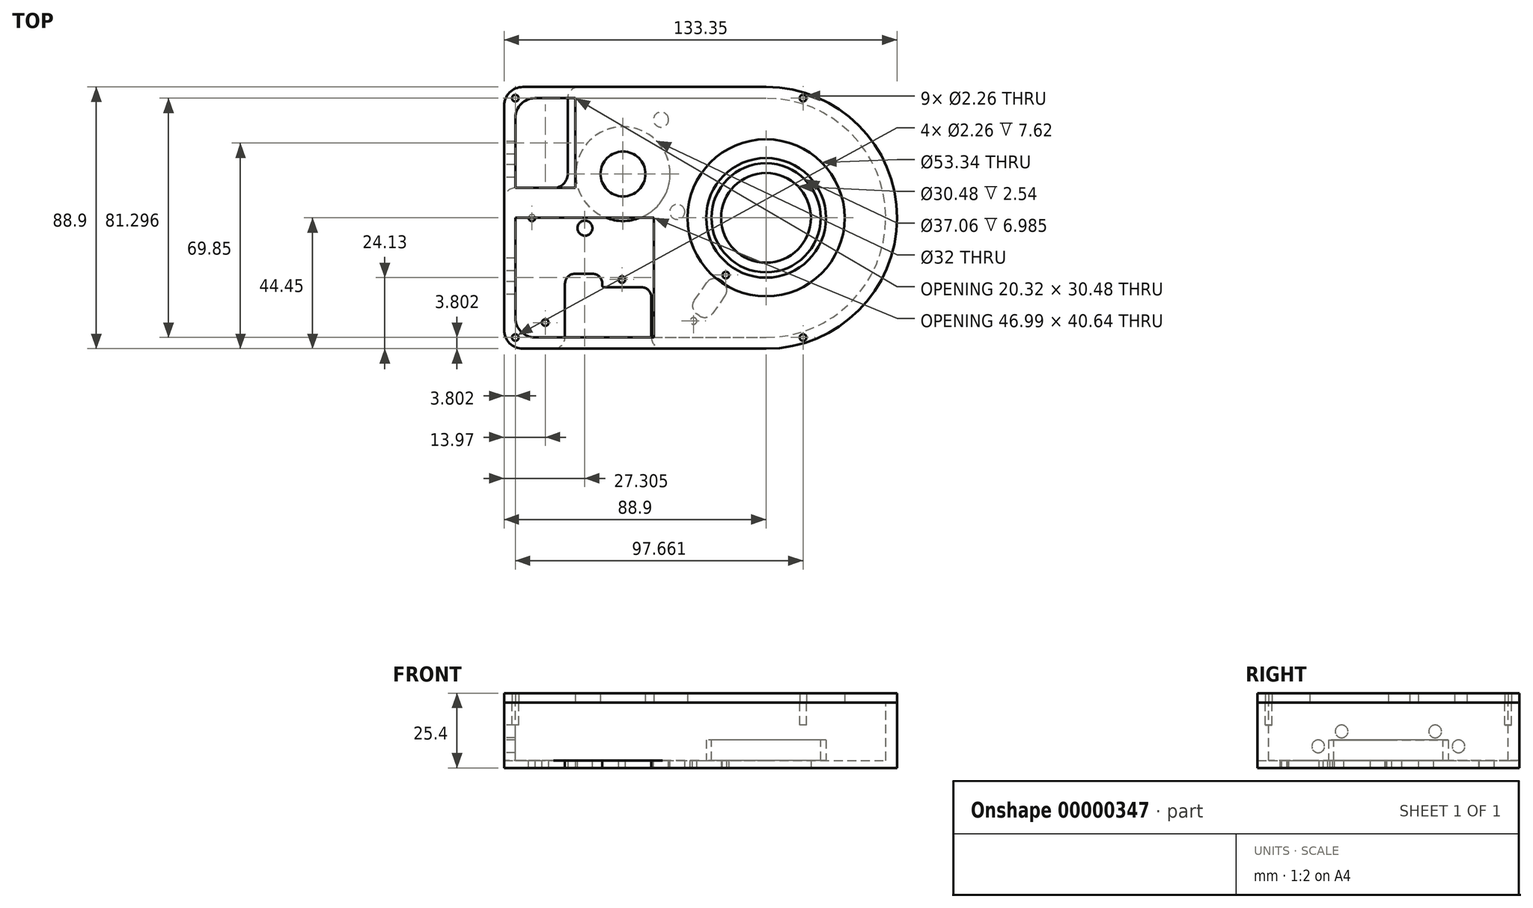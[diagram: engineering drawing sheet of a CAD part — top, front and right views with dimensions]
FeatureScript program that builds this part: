
annotation { "Feature Type Name" : "Feature", "Feature Type Description" : "" }
export const myFeature = defineFeature(function(context is Context, id is Id, definition is map)
    precondition{}
    {
        {
            var Q0;
            Q0=qCreatedBy(makeId("Top.planeOp"),FACE);
            var sketch = newSketch(context, id + "F0", { "sketchPlane" : qUnion([Q0])});
            skLineSegment(sketch, "E0.bottom", {"start": v(6.35, 0) * mm, "end": v(88.9, 0) * mm});
            skLineSegment(sketch, "E0.top", {"start": v(6.35, 88.9) * mm, "end": v(88.9, 88.9) * mm});
            skLineSegment(sketch, "E0.left", {"start": v(0, 6.35) * mm, "end": v(0, 82.55) * mm});
            skLineSegment(sketch, "E0.right", {"start": v(88.9, 0) * mm, "end": v(88.9, 88.9) * mm});
            skArc(sketch, "E1", {"start": v(88.9, 0) * mm, "mid": v(133.35, 44.45) * mm, "end": v(88.9, 88.9) * mm});
            skCircle(sketch, "E2", {"center": v(88.9, 44.45) * mm, "radius": 15.24 * mm});
            skPoint(sketch, "E3.visualSharp", {"position": v(0, 88.9) * mm});
            skArc(sketch, "E3.filletArc", {"start": v(6.35, 88.9) * mm, "mid": v(1.86, 87.04) * mm, "end": v(0, 82.55) * mm});
            skPoint(sketch, "E4.visualSharp", {"position": v(0, 0) * mm});
            skArc(sketch, "E4.filletArc", {"start": v(0, 6.35) * mm, "mid": v(1.86, 1.86) * mm, "end": v(6.35, 0) * mm});
            skSolve(sketch);
        }
        {
            var Q0;
            {var subQ4=sQuery(id+"F0.wireOp",EDGE,"E1");var subQ7=sQuery(id+"F0.wireOp",EDGE,"E0.bottom");Q0=qUnion([makeQuery(id+"F0.imprint","IMPRINT",FACE,{"disambiguationData":[TD([[makeQuery(id+"F0.imprint","IMPRINT",EDGE,{"derivedFrom":subQ7}),1.0]])]}),makeQuery(id+"F0.imprint","IMPRINT",FACE,{"disambiguationData":[TD([[makeQuery(id+"F0.imprint","IMPRINT",EDGE,{"derivedFrom":subQ4}),1.0]])]})]);}
            extrude(context, id + "F1", {"entities" : qUnion([Q0]), "depth" : 22.22 * mm});
        }
        {
            var Q0;
            Q0=makeQuery(id+"F1.opExtrude","CAP_FACE",FACE,{"disambiguationData":[OSD([sQuery(id+"F0.wireOp",EDGE,"E0.bottom"),sQuery(id+"F0.wireOp",EDGE,"E0.top"),sQuery(id+"F0.wireOp",EDGE,"E0.left"),sQuery(id+"F0.wireOp",EDGE,"E1"),sQuery(id+"F0.wireOp",EDGE,"E2")])],"isStart":false});
            var sketch = newSketch(context, id + "F2", { "sketchPlane" : qUnion([Q0])});
            skLineSegment(sketch, "E5.0", {"start": v(10.41, 85.1) * mm, "end": v(88.9, 85.1) * mm});
            skLineSegment(sketch, "E5.1", {"start": v(3.8, 10.41) * mm, "end": v(3.8, 78.49) * mm});
            skLineSegment(sketch, "E5.2", {"start": v(10.41, 3.8) * mm, "end": v(88.9, 3.8) * mm});
            skArc(sketch, "E5.3", {"start": v(88.9, 3.8) * mm, "mid": v(129.54, 44.45) * mm, "end": v(88.9, 85.1) * mm});
            skPoint(sketch, "E6.visualSharp", {"position": v(3.8, 85.1) * mm});
            skArc(sketch, "E6.filletArc", {"start": v(10.41, 85.1) * mm, "mid": v(5.74, 83.16) * mm, "end": v(3.8, 78.49) * mm});
            skPoint(sketch, "E7.visualSharp", {"position": v(3.8, 3.8) * mm});
            skArc(sketch, "E7.filletArc", {"start": v(3.8, 10.41) * mm, "mid": v(5.74, 5.74) * mm, "end": v(10.41, 3.8) * mm});
            skSolve(sketch);
        }
        {
            var Q0;
            {var subQ0=makeQuery(id+"F2.imprint","IMPRINT",EDGE,{"derivedFrom":makeQuery(id+"F1.opExtrude","CAP_EDGE",EDGE,{"disambiguationData":[OSD([sQuery(id+"F0.wireOp",EDGE,"E2")])],"isStart":false})});Q0=qUnion([makeQuery(id+"F2.imprint","IMPRINT",FACE,{"disambiguationData":[TD([[subQ0,1.0]])]}),makeQuery(id+"F2.imprint","IMPRINT",FACE,{"disambiguationData":[TD([[makeQuery(id+"F2.imprint","IMPRINT",EDGE,{"derivedFrom":sQuery(id+"F2.wireOp",EDGE,"E5.0")}),-1.0]])]})]);}
            extrude(context, id + "F3", {"entities" : qUnion([Q0]), "operationType" : NewBodyOperationType.REMOVE, "oppositeDirection" : true, "depth" : 19.68 * mm});
        }
        {
            var Q0;
            Q0=makeQuery(id+"F3.boolean.opBoolean","COPY",FACE,{"derivedFrom":makeQuery(id+"F3.opExtrude","CAP_FACE",FACE,{"disambiguationData":[OSD([sQuery(id+"F2.wireOp",EDGE,"E5.0"),sQuery(id+"F2.wireOp",EDGE,"E5.1"),sQuery(id+"F2.wireOp",EDGE,"E5.2"),sQuery(id+"F2.wireOp",EDGE,"E5.3"),sQuery(id+"F2.wireOp",EDGE,"E6.filletArc"),sQuery(id+"F2.wireOp",EDGE,"E7.filletArc")])],"isStart":false})});
            var sketch = newSketch(context, id + "F4", { "sketchPlane" : qUnion([Q0])});
            skArc(sketch, "E8.0", {"start": v(88.9, 3.8) * mm, "mid": v(129.54, 44.45) * mm, "end": v(88.9, 85.1) * mm, "construction": true});
            skCircle(sketch, "E9", {"center": v(88.9, 44.45) * mm, "radius": 20.32 * mm});
            skSolve(sketch);
        }
        {
            var Q0;
            {var subQ0=makeQuery(id+"F4.imprint","IMPRINT",EDGE,{"derivedFrom":makeQuery(id+"F3.boolean.opBoolean","INTERSECT",EDGE,{"derivedFrom":[makeQuery(id+"F1.opExtrude","SWEPT_FACE",FACE,{"disambiguationData":[OSD([sQuery(id+"F0.wireOp",EDGE,"E2")])]}),makeQuery(id+"F3.opExtrude","CAP_FACE",FACE,{"disambiguationData":[OSD([sQuery(id+"F2.wireOp",EDGE,"E5.0"),sQuery(id+"F2.wireOp",EDGE,"E5.1"),sQuery(id+"F2.wireOp",EDGE,"E5.2"),sQuery(id+"F2.wireOp",EDGE,"E5.3"),sQuery(id+"F2.wireOp",EDGE,"E6.filletArc"),sQuery(id+"F2.wireOp",EDGE,"E7.filletArc")])],"isStart":false})]})});Q0=qUnion([makeQuery(id+"F4.imprint","IMPRINT",FACE,{"disambiguationData":[TD([[subQ0,1.0]])]}),makeQuery(id+"F4.imprint","IMPRINT",FACE,{"disambiguationData":[TD([[makeQuery(id+"F4.imprint","IMPRINT",EDGE,{"derivedFrom":sQuery(id+"F4.wireOp",EDGE,"E9")}),1.0]])]})]);}
            extrude(context, id + "F5", {"entities" : qUnion([Q0]), "operationType" : NewBodyOperationType.ADD, "depth" : 7 * mm});
        }
        {
            var Q0;
            Q0=makeQuery(id+"F5.opExtrude","CAP_FACE",FACE,{"disambiguationData":[OSD([sQuery(id+"F4.wireOp",EDGE,"E9")])],"isStart":false});
            var sketch = newSketch(context, id + "F6", { "sketchPlane" : qUnion([Q0])});
            skCircle(sketch, "E10", {"center": v(88.9, 44.45) * mm, "radius": 18.53 * mm});
            skSolve(sketch);
        }
        {
            var Q0;
            Q0=makeQuery(id+"F6.imprint","IMPRINT",FACE,{"disambiguationData":[TD([[makeQuery(id+"F6.imprint","IMPRINT",EDGE,{"derivedFrom":sQuery(id+"F6.wireOp",EDGE,"E10")}),1.0]])]});
            extrude(context, id + "F7", {"entities" : qUnion([Q0]), "operationType" : NewBodyOperationType.REMOVE, "oppositeDirection" : true, "depth" : 7 * mm});
        }
        {
            var Q0;
            Q0=makeQuery(id+"F1.opExtrude","CAP_FACE",FACE,{"disambiguationData":[OSD([sQuery(id+"F0.wireOp",EDGE,"E0.bottom"),sQuery(id+"F0.wireOp",EDGE,"E0.top"),sQuery(id+"F0.wireOp",EDGE,"E0.left"),sQuery(id+"F0.wireOp",EDGE,"E1"),sQuery(id+"F0.wireOp",EDGE,"E2")])],"isStart":false});
            var sketch = newSketch(context, id + "F8", { "sketchPlane" : qUnion([Q0])});
            skLineSegment(sketch, "E11", {"start": v(101.46, 85.1) * mm, "end": v(101.46, 3.8) * mm, "construction": true});
            skCircle(sketch, "E12", {"center": v(101.46, 3.8) * mm, "radius": 1.13 * mm});
            skCircle(sketch, "E13", {"center": v(101.46, 85.1) * mm, "radius": 1.13 * mm});
            skCircle(sketch, "E14", {"center": v(3.8, 85.1) * mm, "radius": 1.13 * mm});
            skCircle(sketch, "E15", {"center": v(3.8, 3.8) * mm, "radius": 1.13 * mm});
            skLineSegment(sketch, "E16", {"start": v(1.86, 87.04) * mm, "end": v(5.74, 83.16) * mm, "construction": true});
            skLineSegment(sketch, "E17", {"start": v(1.86, 1.86) * mm, "end": v(5.74, 5.74) * mm, "construction": true});
            skLineSegment(sketch, "E18", {"start": v(3.8, 85.1) * mm, "end": v(101.46, 85.1) * mm, "construction": true});
            skLineSegment(sketch, "E19", {"start": v(3.8, 3.8) * mm, "end": v(101.46, 3.8) * mm, "construction": true});
            skSolve(sketch);
        }
        {
            var Q0;
            Q0 = qSketchRegion(id + "F8", true);
            extrude(context, id + "F9", {"entities" : qUnion([Q0]), "operationType" : NewBodyOperationType.REMOVE, "oppositeDirection" : true, "depth" : 7.62 * mm});
        }
        {
            var Q0;
            Q0=makeQuery(id+"F3.boolean.opBoolean","COPY",FACE,{"derivedFrom":makeQuery(id+"F3.opExtrude","CAP_FACE",FACE,{"disambiguationData":[OSD([sQuery(id+"F2.wireOp",EDGE,"E5.0"),sQuery(id+"F2.wireOp",EDGE,"E5.1"),sQuery(id+"F2.wireOp",EDGE,"E5.2"),sQuery(id+"F2.wireOp",EDGE,"E5.3"),sQuery(id+"F2.wireOp",EDGE,"E6.filletArc"),sQuery(id+"F2.wireOp",EDGE,"E7.filletArc")])],"isStart":false})});
            var sketch = newSketch(context, id + "F10", { "sketchPlane" : qUnion([Q0])});
            skCircle(sketch, "E20", {"center": v(88.9, 44.45) * mm, "radius": 38.1 * mm, "construction": true});
            skCircle(sketch, "E21", {"center": v(40.34, 59.37) * mm, "radius": 12.7 * mm, "construction": true});
            skCircle(sketch, "E22", {"center": v(40.34, 59.37) * mm, "radius": 16 * mm});
            skCircle(sketch, "E23", {"center": v(40.34, 59.37) * mm, "radius": 22.5 * mm, "construction": true});
            skCircle(sketch, "E24", {"center": v(40.34, 59.37) * mm, "radius": 28.58 * mm, "construction": true});
            skLineSegment(sketch, "E25", {"start": v(21.91, 72.28) * mm, "end": v(58.77, 46.47) * mm, "construction": true});
            skLineSegment(sketch, "E26", {"start": v(27.43, 40.95) * mm, "end": v(53.25, 77.8) * mm, "construction": true});
            skCircle(sketch, "E27", {"center": v(53.25, 77.8) * mm, "radius": 2.55 * mm});
            skCircle(sketch, "E28", {"center": v(21.91, 72.28) * mm, "radius": 2.55 * mm, "construction": true});
            skCircle(sketch, "E29", {"center": v(27.43, 40.95) * mm, "radius": 2.55 * mm});
            skCircle(sketch, "E30", {"center": v(58.77, 46.47) * mm, "radius": 2.55 * mm});
            skLineSegment(sketch, "E31", {"start": v(88.9, 44.45) * mm, "end": v(61.6, 5.58) * mm, "construction": true});
            skCircle(sketch, "E32", {"center": v(75.25, 25.02) * mm, "radius": 1.13 * mm});
            skCircle(sketch, "E33", {"center": v(64.3, 9.43) * mm, "radius": 1.13 * mm});
            skLineSegment(sketch, "E34", {"start": v(60.1, 8.97) * mm, "end": v(74.26, 29.13) * mm, "construction": true});
            skLineSegment(sketch, "E35", {"start": v(74.26, 29.13) * mm, "end": v(79.45, 25.48) * mm, "construction": true});
            skLineSegment(sketch, "E36", {"start": v(79.45, 25.48) * mm, "end": v(65.29, 5.32) * mm, "construction": true});
            skLineSegment(sketch, "E37", {"start": v(65.29, 5.32) * mm, "end": v(60.1, 8.97) * mm, "construction": true});
            skLineSegment(sketch, "E38", {"start": v(72.37, 15.4) * mm, "end": v(67.17, 19.05) * mm, "construction": true});
            skLineSegment(sketch, "E39", {"start": v(64.54, 16.4) * mm, "end": v(68.77, 22.43) * mm});
            skLineSegment(sketch, "E40", {"start": v(73.37, 23.23) * mm, "end": v(74.2, 22.65) * mm});
            skLineSegment(sketch, "E41", {"start": v(75, 18.05) * mm, "end": v(70.77, 12.02) * mm});
            skLineSegment(sketch, "E42", {"start": v(66.17, 11.22) * mm, "end": v(65.34, 11.8) * mm});
            skPoint(sketch, "E43.visualSharp", {"position": v(70.67, 25.13) * mm});
            skArc(sketch, "E43.filletArc", {"start": v(73.37, 23.23) * mm, "mid": v(70.9, 23.78) * mm, "end": v(68.77, 22.43) * mm});
            skPoint(sketch, "E44.visualSharp", {"position": v(76.9, 20.75) * mm});
            skArc(sketch, "E44.filletArc", {"start": v(75, 18.05) * mm, "mid": v(75.56, 20.51) * mm, "end": v(74.2, 22.65) * mm});
            skPoint(sketch, "E45.visualSharp", {"position": v(68.87, 9.32) * mm});
            skArc(sketch, "E45.filletArc", {"start": v(66.17, 11.22) * mm, "mid": v(68.64, 10.66) * mm, "end": v(70.77, 12.02) * mm});
            skPoint(sketch, "E46.visualSharp", {"position": v(62.64, 13.7) * mm});
            skArc(sketch, "E46.filletArc", {"start": v(64.54, 16.4) * mm, "mid": v(63.99, 13.93) * mm, "end": v(65.34, 11.8) * mm});
            skSolve(sketch);
        }
        {
            var Q0;
            Q0 = qSketchRegion(id + "F10", true);
            extrude(context, id + "F11", {"entities" : qUnion([Q0]), "operationType" : NewBodyOperationType.REMOVE, "oppositeDirection" : true, "depth" : 25.4 * mm});
        }
        {
            var Q0;
            Q0=makeQuery(id+"F1.opExtrude","CAP_FACE",FACE,{"disambiguationData":[OSD([sQuery(id+"F0.wireOp",EDGE,"E0.bottom"),sQuery(id+"F0.wireOp",EDGE,"E0.top"),sQuery(id+"F0.wireOp",EDGE,"E0.left"),sQuery(id+"F0.wireOp",EDGE,"E1"),sQuery(id+"F0.wireOp",EDGE,"E2")])],"isStart":false});
            var sketch = newSketch(context, id + "F12", { "sketchPlane" : qUnion([Q0])});
            skLineSegment(sketch, "E47.0", {"start": v(6.35, 88.9) * mm, "end": v(88.9, 88.9) * mm});
            skArc(sketch, "E48.0", {"start": v(88.9, 0) * mm, "mid": v(133.35, 44.45) * mm, "end": v(88.9, 88.9) * mm});
            skLineSegment(sketch, "E49.0", {"start": v(6.35, 0) * mm, "end": v(88.9, 0) * mm});
            skArc(sketch, "E50.0", {"start": v(0, 6.35) * mm, "mid": v(1.86, 1.86) * mm, "end": v(6.35, 0) * mm});
            skLineSegment(sketch, "E51.0", {"start": v(0, 6.35) * mm, "end": v(0, 82.55) * mm});
            skArc(sketch, "E52.0", {"start": v(6.35, 88.9) * mm, "mid": v(1.86, 87.04) * mm, "end": v(0, 82.55) * mm});
            skCircle(sketch, "E53.0", {"center": v(3.8, 85.1) * mm, "radius": 1.13 * mm});
            skCircle(sketch, "E54.0", {"center": v(101.46, 85.1) * mm, "radius": 1.13 * mm});
            skLineSegment(sketch, "E55.0.3", {"start": v(88.9, 88.9) * mm, "end": v(6.35, 88.9) * mm});
            skLineSegment(sketch, "E55.0.5", {"start": v(0, 82.55) * mm, "end": v(0, 6.35) * mm});
            skCircle(sketch, "E56.0", {"center": v(101.46, 3.8) * mm, "radius": 1.13 * mm});
            skCircle(sketch, "E57.0", {"center": v(3.8, 3.8) * mm, "radius": 1.13 * mm});
            skCircle(sketch, "E58", {"center": v(88.9, 44.45) * mm, "radius": 26.67 * mm});
            skCircle(sketch, "E59", {"center": v(40.34, 59.37) * mm, "radius": 7.62 * mm});
            skLineSegment(sketch, "E60.0", {"start": v(10.41, 3.8) * mm, "end": v(88.9, 3.8) * mm});
            skArc(sketch, "E61.0", {"start": v(3.8, 10.41) * mm, "mid": v(5.74, 5.74) * mm, "end": v(10.41, 3.8) * mm});
            skLineSegment(sketch, "E62.0", {"start": v(3.8, 10.41) * mm, "end": v(3.8, 78.49) * mm});
            skArc(sketch, "E63.0", {"start": v(10.41, 85.1) * mm, "mid": v(5.74, 83.16) * mm, "end": v(3.8, 78.49) * mm});
            skLineSegment(sketch, "E64.0", {"start": v(10.41, 85.1) * mm, "end": v(88.9, 85.1) * mm});
            skLineSegment(sketch, "E65", {"start": v(3.8, 44.45) * mm, "end": v(50.8, 44.45) * mm});
            skLineSegment(sketch, "E66", {"start": v(50.8, 44.45) * mm, "end": v(50.8, 3.8) * mm});
            skCircle(sketch, "E67", {"center": v(88.9, 44.45) * mm, "radius": 38.1 * mm, "construction": true});
            skLineSegment(sketch, "E68", {"start": v(3.8, 54.61) * mm, "end": v(24.13, 54.61) * mm});
            skLineSegment(sketch, "E69", {"start": v(24.13, 54.61) * mm, "end": v(24.13, 85.1) * mm});
            skSolve(sketch);
        }
        {
            var Q0;
            Q0 = qSketchRegion(id + "F12", true);
            extrude(context, id + "F13", {"entities" : qUnion([Q0]), "depth" : 3.17 * mm});
        }
        {
            var Q0;
            Q0=makeQuery(id+"F1.opExtrude","SWEPT_FACE",FACE,{"disambiguationData":[OSD([sQuery(id+"F0.wireOp",EDGE,"E0.left")])]});
            var sketch = newSketch(context, id + "F14", { "sketchPlane" : qUnion([Q0])});
            skCircle(sketch, "E70", {"center": v(-68.26, 7.3) * mm, "radius": 2.16 * mm});
            skCircle(sketch, "E71", {"center": v(-20.64, 7.3) * mm, "radius": 2.16 * mm});
            skCircle(sketch, "E72", {"center": v(-60.33, 12.38) * mm, "radius": 2.16 * mm});
            skCircle(sketch, "E73", {"center": v(-28.58, 12.38) * mm, "radius": 2.16 * mm});
            skSolve(sketch);
        }
        {
            var Q0;
            {Q0=qUnion([makeQuery(id+"F14.imprint","IMPRINT",FACE,{"disambiguationData":[TD([[makeQuery(id+"F14.imprint","IMPRINT",EDGE,{"derivedFrom":sQuery(id+"F14.wireOp",EDGE,"E70")}),1.0]])]}),makeQuery(id+"F14.imprint","IMPRINT",FACE,{"disambiguationData":[TD([[makeQuery(id+"F14.imprint","IMPRINT",EDGE,{"derivedFrom":sQuery(id+"F14.wireOp",EDGE,"E71")}),1.0]])]}),makeQuery(id+"F14.imprint","IMPRINT",FACE,{"disambiguationData":[TD([[makeQuery(id+"F14.imprint","IMPRINT",EDGE,{"derivedFrom":sQuery(id+"F14.wireOp",EDGE,"E72")}),1.0]])]}),makeQuery(id+"F14.imprint","IMPRINT",FACE,{"disambiguationData":[TD([[makeQuery(id+"F14.imprint","IMPRINT",EDGE,{"derivedFrom":sQuery(id+"F14.wireOp",EDGE,"E73")}),1.0]])]})]);}
            var Q1;
            Q1=makeQuery(id+"F3.boolean.opBoolean","COPY",FACE,{"derivedFrom":makeQuery(id+"F3.opExtrude","SWEPT_FACE",FACE,{"disambiguationData":[OSD([sQuery(id+"F2.wireOp",EDGE,"E5.1")])]})});
            extrude(context, id + "F15", {"entities" : qUnion([Q0]), "operationType" : NewBodyOperationType.REMOVE, "endBound" : BoundingType.UP_TO_SURFACE, "oppositeDirection" : true, "endBoundEntityFace" : qUnion([Q1]), "depth" : 25.4 * mm});
        }
        {
            var Q0;
            Q0=makeQuery(id+"F1.opExtrude","CAP_FACE",FACE,{"disambiguationData":[OSD([sQuery(id+"F0.wireOp",EDGE,"E0.bottom"),sQuery(id+"F0.wireOp",EDGE,"E0.top"),sQuery(id+"F0.wireOp",EDGE,"E0.left"),sQuery(id+"F0.wireOp",EDGE,"E1"),sQuery(id+"F0.wireOp",EDGE,"E2")])],"isStart":true});
            var sketch = newSketch(context, id + "F16", { "sketchPlane" : qUnion([Q0])});
            skCircle(sketch, "E74", {"center": v(88.9, -44.45) * mm, "radius": 28.57 * mm, "construction": true});
            skLineSegment(sketch, "E75.bottom", {"start": v(60.32, -73.03) * mm, "end": v(117.47, -73.03) * mm, "construction": true});
            skLineSegment(sketch, "E75.top", {"start": v(60.32, -15.88) * mm, "end": v(117.47, -15.88) * mm, "construction": true});
            skLineSegment(sketch, "E75.left", {"start": v(60.32, -73.03) * mm, "end": v(60.32, -15.88) * mm, "construction": true});
            skLineSegment(sketch, "E75.right", {"start": v(117.47, -73.03) * mm, "end": v(117.47, -15.88) * mm, "construction": true});
            skCircle(sketch, "E76", {"center": v(65.09, -68.26) * mm, "radius": 2.16 * mm});
            skCircle(sketch, "E77", {"center": v(65.09, -20.64) * mm, "radius": 2.16 * mm});
            skSolve(sketch);
        }
        {
            var Q0;
            Q0=makeQuery(id+"F3.boolean.opBoolean","COPY",FACE,{"derivedFrom":makeQuery(id+"F3.opExtrude","CAP_FACE",FACE,{"disambiguationData":[OSD([sQuery(id+"F2.wireOp",EDGE,"E5.0"),sQuery(id+"F2.wireOp",EDGE,"E5.1"),sQuery(id+"F2.wireOp",EDGE,"E5.2"),sQuery(id+"F2.wireOp",EDGE,"E5.3"),sQuery(id+"F2.wireOp",EDGE,"E6.filletArc"),sQuery(id+"F2.wireOp",EDGE,"E7.filletArc")])],"isStart":false})});
            var sketch = newSketch(context, id + "F17", { "sketchPlane" : qUnion([Q0])});
            skCircle(sketch, "E78", {"center": v(9.45, 44.45) * mm, "radius": 1.13 * mm});
            skCircle(sketch, "E79.cCircle", {"center": v(9.45, 44.45) * mm, "radius": 3.67 * mm, "construction": true});
            skLineSegment(sketch, "E79.0", {"start": v(12.07, 41.89) * mm, "end": v(8.54, 40.9) * mm, "construction": true});
            skLineSegment(sketch, "E79.1", {"start": v(8.54, 40.9) * mm, "end": v(5.92, 43.46) * mm, "construction": true});
            skLineSegment(sketch, "E79.2", {"start": v(5.92, 43.46) * mm, "end": v(6.83, 47.01) * mm, "construction": true});
            skLineSegment(sketch, "E79.3", {"start": v(6.83, 47.01) * mm, "end": v(10.36, 48) * mm, "construction": true});
            skLineSegment(sketch, "E79.4", {"start": v(10.36, 48) * mm, "end": v(12.98, 45.44) * mm, "construction": true});
            skLineSegment(sketch, "E79.5", {"start": v(12.98, 45.44) * mm, "end": v(12.07, 41.89) * mm, "construction": true});
            skCircle(sketch, "E80", {"center": v(13.96, 8.86) * mm, "radius": 1.13 * mm});
            skCircle(sketch, "E81", {"center": v(40, 23.48) * mm, "radius": 1.13 * mm});
            skSolve(sketch);
        }
        {
            var Q0;
            Q0 = qSketchRegion(id + "F17", true);
            extrude(context, id + "F18", {"entities" : qUnion([Q0]), "operationType" : NewBodyOperationType.REMOVE, "endBound" : BoundingType.THROUGH_ALL, "oppositeDirection" : true, "depth" : 25.4 * mm});
        }
        {
            var Q0;
            Q0=makeQuery(id+"F1.opExtrude","CAP_FACE",FACE,{"disambiguationData":[OSD([sQuery(id+"F0.wireOp",EDGE,"E0.bottom"),sQuery(id+"F0.wireOp",EDGE,"E0.top"),sQuery(id+"F0.wireOp",EDGE,"E0.left"),sQuery(id+"F0.wireOp",EDGE,"E1"),sQuery(id+"F0.wireOp",EDGE,"E2"),sQuery(id+"F0.wireOp",EDGE,"E3.filletArc"),sQuery(id+"F0.wireOp",EDGE,"E4.filletArc")])],"isStart":true});
            var sketch = newSketch(context, id + "F19", { "sketchPlane" : qUnion([Q0])});
            skLineSegment(sketch, "E82.top", {"start": v(16.76, -54.61) * mm, "end": v(3.8, -54.61) * mm});
            skLineSegment(sketch, "E82.left", {"start": v(21.59, -85.1) * mm, "end": v(21.59, -59.44) * mm});
            skLineSegment(sketch, "E83.0", {"start": v(21.59, -85.1) * mm, "end": v(88.9, -85.1) * mm, "construction": true});
            skLineSegment(sketch, "E84.0", {"start": v(10.41, -3.8) * mm, "end": v(88.9, -3.8) * mm, "construction": true});
            skLineSegment(sketch, "E85.0", {"start": v(3.8, -10.41) * mm, "end": v(3.8, -54.61) * mm, "construction": true});
            skLineSegment(sketch, "E86", {"start": v(25.4, -88.9) * mm, "end": v(25.4, -88.9) * mm});
            skLineSegment(sketch, "E87", {"start": v(0, -50.8) * mm, "end": v(0, -50.8) * mm});
            skLineSegment(sketch, "E88", {"start": v(21.59, -85.1) * mm, "end": v(21.59, -85.1) * mm});
            skLineSegment(sketch, "E89", {"start": v(3.8, -54.61) * mm, "end": v(3.81, -54.61) * mm});
            skPoint(sketch, "E90.orphan", {"position": v(3.8, -78.49) * mm});
            skLineSegment(sketch, "E91.0", {"start": v(0, -50.8) * mm, "end": v(0, -82.55) * mm});
            skArc(sketch, "E92.0", {"start": v(6.35, -88.9) * mm, "mid": v(1.86, -87.04) * mm, "end": v(0, -82.55) * mm});
            skLineSegment(sketch, "E93.0", {"start": v(6.35, -88.9) * mm, "end": v(25.4, -88.9) * mm});
            skPoint(sketch, "E94.orphan", {"position": v(0, -6.35) * mm});
            skPoint(sketch, "E95.orphan", {"position": v(88.9, -88.9) * mm});
            skPoint(sketch, "E82.bottom.end.orphan", {"position": v(10.41, -85.1) * mm});
            skPoint(sketch, "E96.visualSharp", {"position": v(0, -54.61) * mm});
            skArc(sketch, "E96.filletArc", {"start": v(0, -50.8) * mm, "mid": v(1.12, -53.5) * mm, "end": v(3.81, -54.61) * mm});
            skPoint(sketch, "E97.visualSharp", {"position": v(21.59, -88.9) * mm});
            skArc(sketch, "E97.filletArc", {"start": v(21.59, -85.1) * mm, "mid": v(22.7, -87.78) * mm, "end": v(25.4, -88.9) * mm});
            skPoint(sketch, "E98.visualSharp", {"position": v(21.59, -54.61) * mm});
            skArc(sketch, "E98.filletArc", {"start": v(21.59, -59.44) * mm, "mid": v(20.18, -56.02) * mm, "end": v(16.76, -54.61) * mm});
            skLineSegment(sketch, "E99.bottom", {"start": v(20.65, 0) * mm, "end": v(49.99, 0) * mm});
            skLineSegment(sketch, "E99.top", {"start": v(33.86, -20.83) * mm, "end": v(46.69, -20.83) * mm});
            skLineSegment(sketch, "E99.left", {"start": v(20.65, -3.8) * mm, "end": v(20.65, -20.83) * mm});
            skLineSegment(sketch, "E99.right", {"start": v(49.99, -3.81) * mm, "end": v(49.99, -17.53) * mm});
            skLineSegment(sketch, "E100.top", {"start": v(23.95, -25.4) * mm, "end": v(30.05, -25.4) * mm});
            skLineSegment(sketch, "E100.left", {"start": v(20.65, -20.83) * mm, "end": v(20.65, -22.1) * mm});
            skLineSegment(sketch, "E100.right", {"start": v(33.35, -21.34) * mm, "end": v(33.35, -22.1) * mm});
            skPoint(sketch, "E101.visualSharp", {"position": v(20.65, -25.4) * mm});
            skArc(sketch, "E101.filletArc", {"start": v(20.65, -22.1) * mm, "mid": v(21.62, -24.43) * mm, "end": v(23.95, -25.4) * mm});
            skPoint(sketch, "E102.visualSharp", {"position": v(33.35, -25.4) * mm});
            skArc(sketch, "E102.filletArc", {"start": v(30.05, -25.4) * mm, "mid": v(32.38, -24.43) * mm, "end": v(33.35, -22.1) * mm});
            skLineSegment(sketch, "E103", {"start": v(16.84, 0) * mm, "end": v(16.84, 0) * mm});
            skLineSegment(sketch, "E104", {"start": v(53.8, 0) * mm, "end": v(53.8, 0) * mm});
            skPoint(sketch, "E105.visualSharp", {"position": v(20.65, 0) * mm});
            skArc(sketch, "E105.filletArc", {"start": v(20.65, -3.8) * mm, "mid": v(19.53, -1.12) * mm, "end": v(16.84, 0) * mm});
            skPoint(sketch, "E106.visualSharp", {"position": v(49.99, 0) * mm});
            skArc(sketch, "E106.filletArc", {"start": v(53.8, 0) * mm, "mid": v(51.1, -1.12) * mm, "end": v(49.99, -3.8) * mm});
            skLineSegment(sketch, "E107", {"start": v(16.84, 0) * mm, "end": v(53.8, 0) * mm});
            skPoint(sketch, "E108.visualSharp", {"position": v(33.35, -20.83) * mm});
            skArc(sketch, "E108.filletArc", {"start": v(33.86, -20.83) * mm, "mid": v(33.5, -20.98) * mm, "end": v(33.35, -21.34) * mm});
            skPoint(sketch, "E109.visualSharp", {"position": v(49.99, -20.83) * mm});
            skArc(sketch, "E109.filletArc", {"start": v(46.69, -20.83) * mm, "mid": v(49.02, -19.86) * mm, "end": v(49.99, -17.53) * mm});
            skSolve(sketch);
        }
        {
            var Q0;
            Q0 = qSketchRegion(id + "F19", true);
            extrude(context, id + "F20", {"entities" : qUnion([Q0]), "operationType" : NewBodyOperationType.REMOVE, "oppositeDirection" : true, "depth" : 2.54 * mm});
        }
    });
